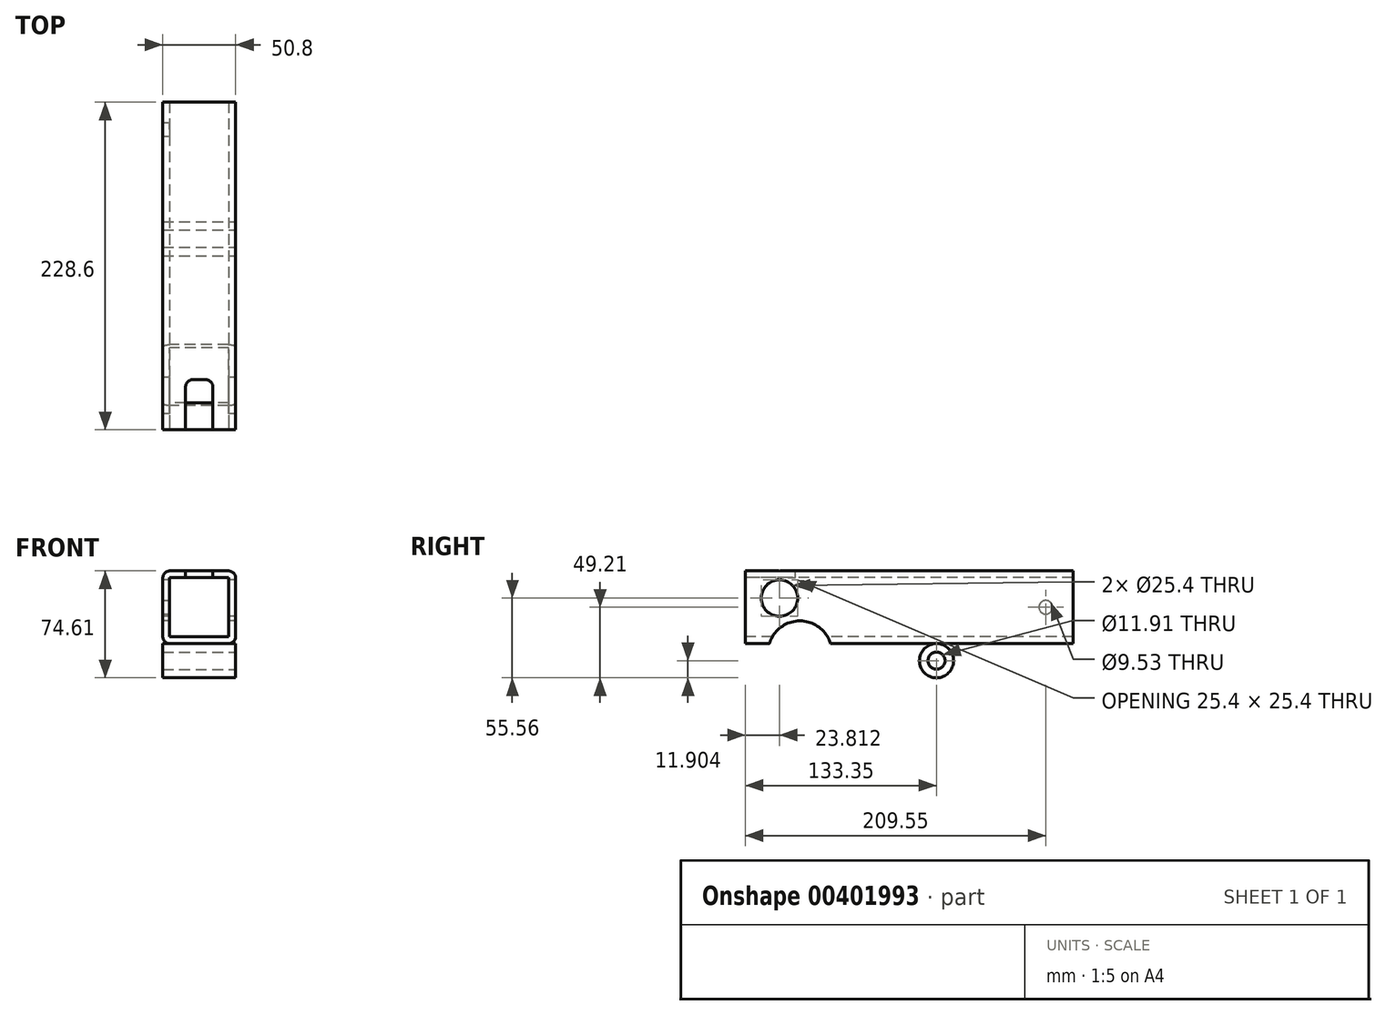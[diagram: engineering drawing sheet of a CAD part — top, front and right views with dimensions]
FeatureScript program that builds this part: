
annotation { "Feature Type Name" : "Feature", "Feature Type Description" : "" }
export const myFeature = defineFeature(function(context is Context, id is Id, definition is map)
    precondition{}
    {
        {
            var Q0;
            Q0=qCreatedBy(makeId("Front.planeOp"),FACE);
            var sketch = newSketch(context, id + "F0", { "sketchPlane" : qUnion([Q0])});
            skLineSegment(sketch, "E0.bottom", {"start": v(25.4, 25.4) * mm, "end": v(-25.4, 25.4) * mm});
            skLineSegment(sketch, "E0.top", {"start": v(25.4, -25.4) * mm, "end": v(-25.4, -25.4) * mm});
            skLineSegment(sketch, "E0.left", {"start": v(25.4, 25.4) * mm, "end": v(25.4, -25.4) * mm});
            skLineSegment(sketch, "E0.right", {"start": v(-25.4, 25.4) * mm, "end": v(-25.4, -25.4) * mm});
            skPoint(sketch, "E0.middle", {"position": v(0, 0) * mm});
            skLineSegment(sketch, "E1.bottom", {"start": v(20.64, 20.64) * mm, "end": v(-20.64, 20.64) * mm});
            skLineSegment(sketch, "E1.top", {"start": v(20.64, -20.64) * mm, "end": v(-20.64, -20.64) * mm});
            skLineSegment(sketch, "E1.left", {"start": v(20.64, 20.64) * mm, "end": v(20.64, -20.64) * mm});
            skLineSegment(sketch, "E1.right", {"start": v(-20.64, 20.64) * mm, "end": v(-20.64, -20.64) * mm});
            skSolve(sketch);
        }
        {
            var Q0;
            Q0=makeQuery(id+"F0.imprint","IMPRINT",FACE,{"disambiguationData":[TD([[makeQuery(id+"F0.imprint","IMPRINT",EDGE,{"derivedFrom":sQuery(id+"F0.wireOp",EDGE,"E0.bottom")}),1.0]])]});
            extrude(context, id + "F1", {"entities" : qUnion([Q0]), "oppositeDirection" : true, "depth" : 228.6 * mm});
        }
        {
            var Q0;
            Q0=qCreatedBy(makeId("Right.planeOp"),FACE);
            var sketch = newSketch(context, id + "F2", { "sketchPlane" : qUnion([Q0])});
            skCircle(sketch, "E2", {"center": v(133.35, -38.1) * mm, "radius": 12.7 * mm});
            skCircle(sketch, "E3", {"center": v(133.35, -38.1) * mm, "radius": 5.95 * mm});
            skCircle(sketch, "E4", {"center": v(23.81, 6.35) * mm, "radius": 12.7 * mm});
            skCircle(sketch, "E5", {"center": v(38.1, -31.75) * mm, "radius": 22.23 * mm});
            skSolve(sketch);
        }
        {
            var Q0;
            Q0=makeQuery(id+"F2.imprint","IMPRINT",FACE,{"disambiguationData":[TD([[makeQuery(id+"F2.imprint","IMPRINT",EDGE,{"derivedFrom":sQuery(id+"F2.wireOp",EDGE,"E5")}),1.0]])]});
            var Q1;
            Q1=makeQuery(id+"F2.imprint","IMPRINT",FACE,{"disambiguationData":[TD([[makeQuery(id+"F2.imprint","IMPRINT",EDGE,{"derivedFrom":sQuery(id+"F2.wireOp",EDGE,"E4")}),1.0]])]});
            extrude(context, id + "F3", {"entities" : qUnion([Q0, Q1]), "operationType" : NewBodyOperationType.REMOVE, "depth" : 50.8 * mm, "symmetric" : true});
        }
        {
            var Q0;
            Q0=makeQuery(id+"F1.opExtrude","SWEPT_FACE",FACE,{"disambiguationData":[OSD([sQuery(id+"F0.wireOp",EDGE,"E0.left")])]});
            var sketch = newSketch(context, id + "F4", { "sketchPlane" : qUnion([Q0])});
            skCircle(sketch, "E6", {"center": v(133.35, -37.3) * mm, "radius": 11.9 * mm});
            skCircle(sketch, "E7", {"center": v(133.35, -37.3) * mm, "radius": 5.95 * mm});
            skSolve(sketch);
        }
        {
            var Q0;
            Q0=makeQuery(id+"F4.imprint","IMPRINT",FACE,{"disambiguationData":[TD([[makeQuery(id+"F4.imprint","IMPRINT",EDGE,{"derivedFrom":sQuery(id+"F4.wireOp",EDGE,"E6")}),1.0]])]});
            extrude(context, id + "F5", {"entities" : qUnion([Q0]), "operationType" : NewBodyOperationType.ADD, "oppositeDirection" : true, "depth" : 50.8 * mm});
        }
        {
            var Q0;
            Q0=makeQuery(id+"F1.opExtrude","SWEPT_EDGE",EDGE,{"disambiguationData":[OSD([sQuery(id+"F0.wireOp",EDGE,"E0.bottom"),sQuery(id+"F0.wireOp",EDGE,"E0.left")])]});
            var Q1;
            Q1=makeQuery(id+"F1.opExtrude","SWEPT_EDGE",EDGE,{"disambiguationData":[OSD([sQuery(id+"F0.wireOp",EDGE,"E0.bottom"),sQuery(id+"F0.wireOp",EDGE,"E0.right")])]});
            var Q2;
            {var subQ0=sQuery(id+"F0.wireOp",EDGE,"E0.left");var subQ1=sQuery(id+"F0.wireOp",EDGE,"E0.top");Q2=makeQuery(id+"F3.boolean.opBoolean","SPLIT",EDGE,{"disambiguationData":[TD([makeQuery(id+"F1.opExtrude","CAP_FACE",FACE,{"disambiguationData":[OSD([sQuery(id+"F0.wireOp",EDGE,"E0.bottom"),subQ1,subQ0,sQuery(id+"F0.wireOp",EDGE,"E0.right"),sQuery(id+"F0.wireOp",EDGE,"E1.bottom"),sQuery(id+"F0.wireOp",EDGE,"E1.top"),sQuery(id+"F0.wireOp",EDGE,"E1.left"),sQuery(id+"F0.wireOp",EDGE,"E1.right")])],"isStart":false})])],"derivedFrom":makeQuery(id+"F1.opExtrude","SWEPT_EDGE",EDGE,{"disambiguationData":[OSD([subQ1,subQ0])]})});}
            var Q3;
            {var subQ0=sQuery(id+"F0.wireOp",EDGE,"E0.right");var subQ1=sQuery(id+"F0.wireOp",EDGE,"E0.top");Q3=makeQuery(id+"F3.boolean.opBoolean","SPLIT",EDGE,{"disambiguationData":[TD([makeQuery(id+"F1.opExtrude","CAP_FACE",FACE,{"disambiguationData":[OSD([sQuery(id+"F0.wireOp",EDGE,"E0.bottom"),subQ1,sQuery(id+"F0.wireOp",EDGE,"E0.left"),subQ0,sQuery(id+"F0.wireOp",EDGE,"E1.bottom"),sQuery(id+"F0.wireOp",EDGE,"E1.top"),sQuery(id+"F0.wireOp",EDGE,"E1.left"),sQuery(id+"F0.wireOp",EDGE,"E1.right")])],"isStart":false})])],"derivedFrom":makeQuery(id+"F1.opExtrude","SWEPT_EDGE",EDGE,{"disambiguationData":[OSD([subQ1,subQ0])]})});}
            var Q4;
            {var subQ0=sQuery(id+"F0.wireOp",EDGE,"E0.left");var subQ1=sQuery(id+"F0.wireOp",EDGE,"E0.top");Q4=makeQuery(id+"F3.boolean.opBoolean","SPLIT",EDGE,{"disambiguationData":[TD([makeQuery(id+"F1.opExtrude","CAP_FACE",FACE,{"disambiguationData":[OSD([sQuery(id+"F0.wireOp",EDGE,"E0.bottom"),subQ1,subQ0,sQuery(id+"F0.wireOp",EDGE,"E0.right"),sQuery(id+"F0.wireOp",EDGE,"E1.bottom"),sQuery(id+"F0.wireOp",EDGE,"E1.top"),sQuery(id+"F0.wireOp",EDGE,"E1.left"),sQuery(id+"F0.wireOp",EDGE,"E1.right")])],"isStart":true})])],"derivedFrom":makeQuery(id+"F1.opExtrude","SWEPT_EDGE",EDGE,{"disambiguationData":[OSD([subQ1,subQ0])]})});}
            var Q5;
            {var subQ0=sQuery(id+"F0.wireOp",EDGE,"E0.right");var subQ1=sQuery(id+"F0.wireOp",EDGE,"E0.top");Q5=makeQuery(id+"F3.boolean.opBoolean","SPLIT",EDGE,{"disambiguationData":[TD([makeQuery(id+"F1.opExtrude","CAP_FACE",FACE,{"disambiguationData":[OSD([sQuery(id+"F0.wireOp",EDGE,"E0.bottom"),subQ1,sQuery(id+"F0.wireOp",EDGE,"E0.left"),subQ0,sQuery(id+"F0.wireOp",EDGE,"E1.bottom"),sQuery(id+"F0.wireOp",EDGE,"E1.top"),sQuery(id+"F0.wireOp",EDGE,"E1.left"),sQuery(id+"F0.wireOp",EDGE,"E1.right")])],"isStart":true})])],"derivedFrom":makeQuery(id+"F1.opExtrude","SWEPT_EDGE",EDGE,{"disambiguationData":[OSD([subQ1,subQ0])]})});}
            fillet(context, id + "F6", {"entities" : qUnion([Q0, Q1, Q2, Q3, Q4, Q5]), "radius" : 5.08 * mm, "tangentPropagation" : true, "allowEdgeOverflow" : false});
        }
        {
            var Q0;
            Q0=makeQuery(id+"F1.opExtrude","SWEPT_FACE",FACE,{"disambiguationData":[OSD([sQuery(id+"F0.wireOp",EDGE,"E0.bottom")])]});
            var sketch = newSketch(context, id + "F7", { "sketchPlane" : qUnion([Q0])});
            skLineSegment(sketch, "E8.bottom", {"start": v(-9.52, 0) * mm, "end": v(9.53, 0) * mm});
            skLineSegment(sketch, "E8.top", {"start": v(-9.53, 34.92) * mm, "end": v(9.52, 34.92) * mm});
            skLineSegment(sketch, "E8.left", {"start": v(-9.52, 0) * mm, "end": v(-9.53, 34.93) * mm});
            skLineSegment(sketch, "E8.right", {"start": v(9.53, 0) * mm, "end": v(9.52, 34.93) * mm});
            skSolve(sketch);
        }
        {
            var Q0;
            Q0=makeQuery(id+"F7.imprint","IMPRINT",FACE,{"disambiguationData":[TD([[makeQuery(id+"F7.imprint","IMPRINT",EDGE,{"derivedFrom":sQuery(id+"F7.wireOp",EDGE,"E8.bottom")}),-1.0]])]});
            extrude(context, id + "F8", {"entities" : qUnion([Q0]), "operationType" : NewBodyOperationType.REMOVE, "endBound" : BoundingType.UP_TO_NEXT, "oppositeDirection" : true, "depth" : 25.4 * mm});
        }
        {
            var Q0;
            Q0=makeQuery(id+"F8.boolean.opBoolean","COPY",EDGE,{"derivedFrom":makeQuery(id+"F8.opExtrude","SWEPT_EDGE",EDGE,{"disambiguationData":[OSD([sQuery(id+"F7.wireOp",EDGE,"E8.top"),sQuery(id+"F7.wireOp",EDGE,"E8.right")])]})});
            var Q1;
            Q1=makeQuery(id+"F8.boolean.opBoolean","COPY",EDGE,{"derivedFrom":makeQuery(id+"F8.opExtrude","SWEPT_EDGE",EDGE,{"disambiguationData":[OSD([sQuery(id+"F7.wireOp",EDGE,"E8.top"),sQuery(id+"F7.wireOp",EDGE,"E8.left")])]})});
            fillet(context, id + "F9", {"entities" : qUnion([Q0, Q1]), "radius" : 5.08 * mm, "tangentPropagation" : true, "allowEdgeOverflow" : false});
        }
        {
            var Q0;
            Q0=makeQuery(id+"F1.opExtrude","SWEPT_FACE",FACE,{"disambiguationData":[OSD([sQuery(id+"F0.wireOp",EDGE,"E0.right")])]});
            var sketch = newSketch(context, id + "F10", { "sketchPlane" : qUnion([Q0])});
            skPoint(sketch, "E9", {"position": v(-209.55, 0) * mm});
            skSolve(sketch);
        }
        {
            var Q0;
            Q0=sQuery(id+"F10.wireOp",VERTEX,"E9");
            var Q1;
            Q1=makeQuery(id+"F1.opExtrude","SWEPT_BODY",BODY,{"disambiguationData":[OSD([sQuery(id+"F0.wireOp",EDGE,"E0.bottom"),sQuery(id+"F0.wireOp",EDGE,"E0.top"),sQuery(id+"F0.wireOp",EDGE,"E0.left"),sQuery(id+"F0.wireOp",EDGE,"E0.right"),sQuery(id+"F0.wireOp",EDGE,"E1.bottom"),sQuery(id+"F0.wireOp",EDGE,"E1.top"),sQuery(id+"F0.wireOp",EDGE,"E1.left"),sQuery(id+"F0.wireOp",EDGE,"E1.right")])]});
            hole(context, id + "F11", {"style" : HoleStyle.SIMPLE, "endStyle" : HoleEndStyle.BLIND, "holeDiameter" : 9.52 * mm, "holeDepth" : 12.7 * mm, "isTappedThrough" : true, "tappedDepth" : 12.7 * mm, "tapClearance" : 3, "locations" : qUnion([Q0]), "scope" : qUnion([Q1])});
        }
    });
